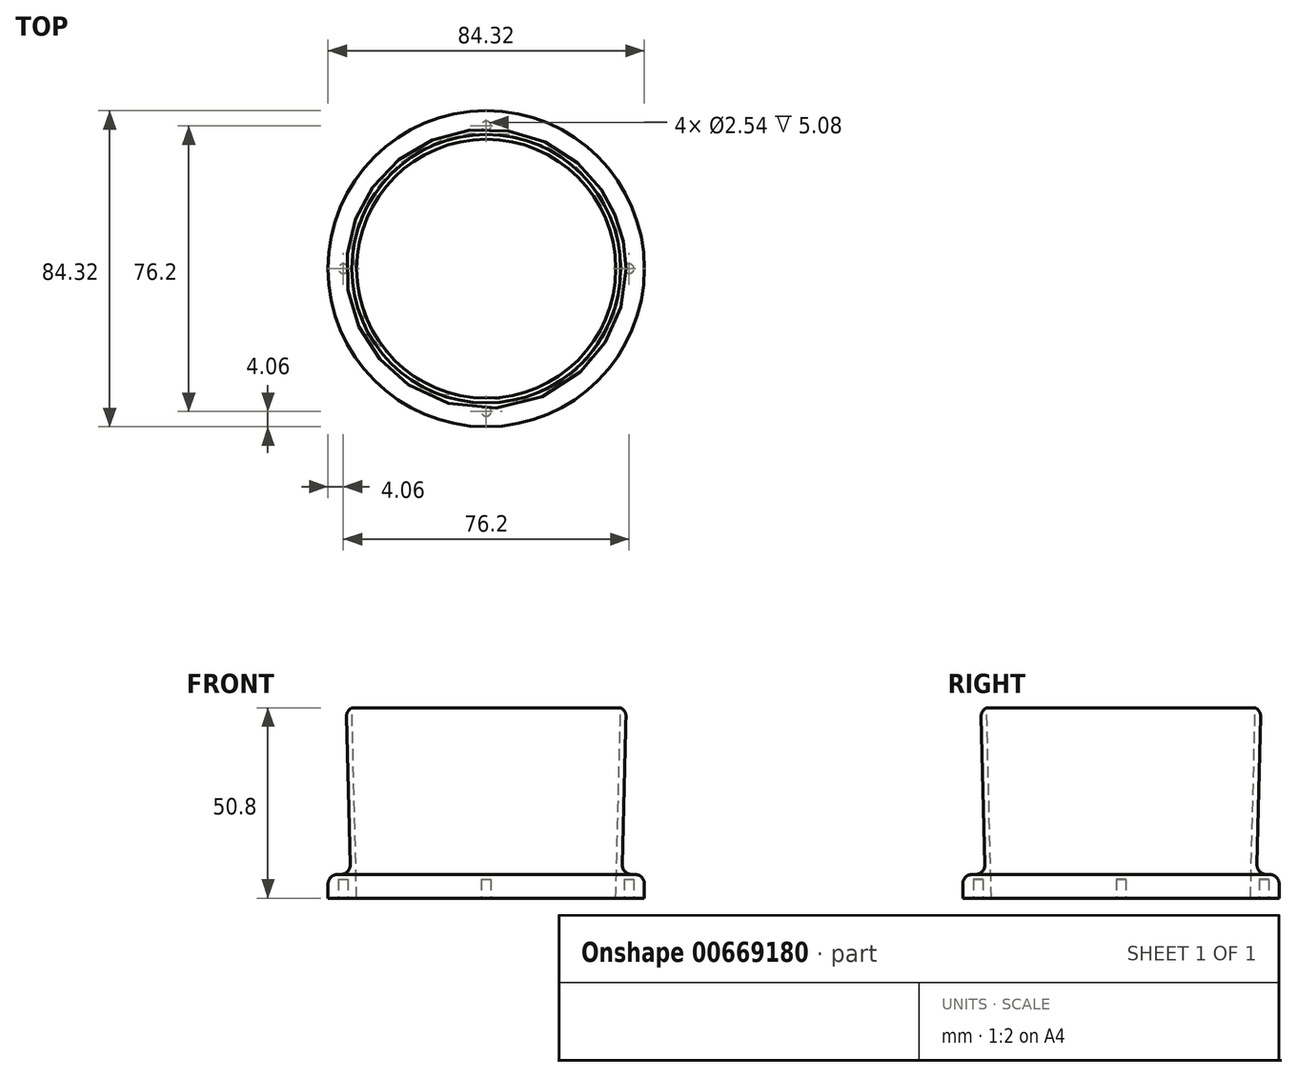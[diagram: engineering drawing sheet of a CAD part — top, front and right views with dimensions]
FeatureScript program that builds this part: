
annotation { "Feature Type Name" : "Feature", "Feature Type Description" : "" }
export const myFeature = defineFeature(function(context is Context, id is Id, definition is map)
    precondition{}
    {
        {
            var Q0;
            Q0=qCreatedBy(makeId("Front.planeOp"),FACE);
            var sketch = newSketch(context, id + "F0", { "sketchPlane" : qUnion([Q0])});
            skLineSegment(sketch, "E0", {"start": v(0, 82.11) * mm, "end": v(0, -65.53) * mm, "construction": true});
            skLineSegment(sketch, "E1", {"start": v(-34.54, 0) * mm, "end": v(-35.81, 50.8) * mm});
            skLineSegment(sketch, "E2", {"start": v(-35.81, 50.8) * mm, "end": v(-37.31, 50.8) * mm});
            skLineSegment(sketch, "E3", {"start": v(-37.31, 50.8) * mm, "end": v(-36.2, 6.35) * mm});
            skLineSegment(sketch, "E4", {"start": v(-36.2, 6.35) * mm, "end": v(-42.16, 6.35) * mm});
            skLineSegment(sketch, "E5", {"start": v(-42.16, 6.35) * mm, "end": v(-42.16, 0) * mm});
            skLineSegment(sketch, "E6", {"start": v(-42.16, 0) * mm, "end": v(-34.54, 0) * mm});
            skLineSegment(sketch, "E7", {"start": v(-34.54, 0) * mm, "end": v(-34.54, -31.75) * mm, "construction": true});
            skLineSegment(sketch, "E8", {"start": v(0, 0) * mm, "end": v(-38.1, 0) * mm, "construction": true});
            skSolve(sketch);
        }
        {
            var Q0;
            Q0=makeQuery(id+"F0.imprint","IMPRINT",FACE,{"disambiguationData":[TD([[makeQuery(id+"F0.imprint","IMPRINT",EDGE,{"derivedFrom":sQuery(id+"F0.wireOp",EDGE,"E1")}),1.0]])]});
            var Q1;
            Q1=sQuery(id+"F0.wireOp",EDGE,"E0");
            revolve(context, id + "F1", {"surfaceOperationType" : NewSurfaceOperationType.NEW, "entities" : qUnion([Q0]), "axis" : qUnion([Q1]), "revolveType" : RevolveType.FULL});
        }
        {
            var Q0;
            Q0=makeQuery(id+"F1.opRevolve","SWEPT_EDGE",EDGE,{"disambiguationData":[OSD([sQuery(id+"F0.wireOp",EDGE,"E3"),sQuery(id+"F0.wireOp",EDGE,"E4")])]});
            var Q1;
            Q1=makeQuery(id+"F1.opRevolve","SWEPT_EDGE",EDGE,{"disambiguationData":[OSD([sQuery(id+"F0.wireOp",EDGE,"E4"),sQuery(id+"F0.wireOp",EDGE,"E5")])]});
            var Q2;
            Q2=makeQuery(id+"F1.opRevolve","SWEPT_EDGE",EDGE,{"disambiguationData":[OSD([sQuery(id+"F0.wireOp",EDGE,"E2"),sQuery(id+"F0.wireOp",EDGE,"E3")])]});
            fillet(context, id + "F2", {"entities" : qUnion([Q0, Q1, Q2]), "tangentPropagation" : true, "radius" : 2.54 * mm, "defaultsChanged" : true, "vertexSettings" : [], "allowEdgeOverflow" : false});
        }
        {
            var Q0;
            Q0=makeQuery(id+"F1.opRevolve","SWEPT_FACE",FACE,{"disambiguationData":[OSD([sQuery(id+"F0.wireOp",EDGE,"E6")])]});
            var sketch = newSketch(context, id + "F3", { "sketchPlane" : qUnion([Q0])});
            skCircle(sketch, "E9", {"center": v(0, 38.1) * mm, "radius": 1.27 * mm});
            skCircle(sketch, "E10.1.0", {"center": v(38.1, 0) * mm, "radius": 1.27 * mm});
            skCircle(sketch, "E10.2.0", {"center": v(0, -38.1) * mm, "radius": 1.27 * mm});
            skCircle(sketch, "E10.3.0", {"center": v(-38.1, 0) * mm, "radius": 1.27 * mm});
            skPoint(sketch, "E10.center", {"position": v(0, 0) * mm});
            skLineSegment(sketch, "E10.anchor1", {"start": v(0, 0) * mm, "end": v(0, 38.1) * mm, "construction": true});
            skLineSegment(sketch, "E10.anchor2", {"start": v(0, 0) * mm, "end": v(-38.1, 0) * mm, "construction": true});
            skSolve(sketch);
        }
        {
            var Q0;
            Q0 = qSketchRegion(id + "F3", true);
            extrude(context, id + "F4", {"entities" : qUnion([Q0]), "operationType" : NewBodyOperationType.REMOVE, "oppositeDirection" : true, "depth" : 5.08 * mm, "offsetDistance" : 25.4 * mm});
        }
    });
